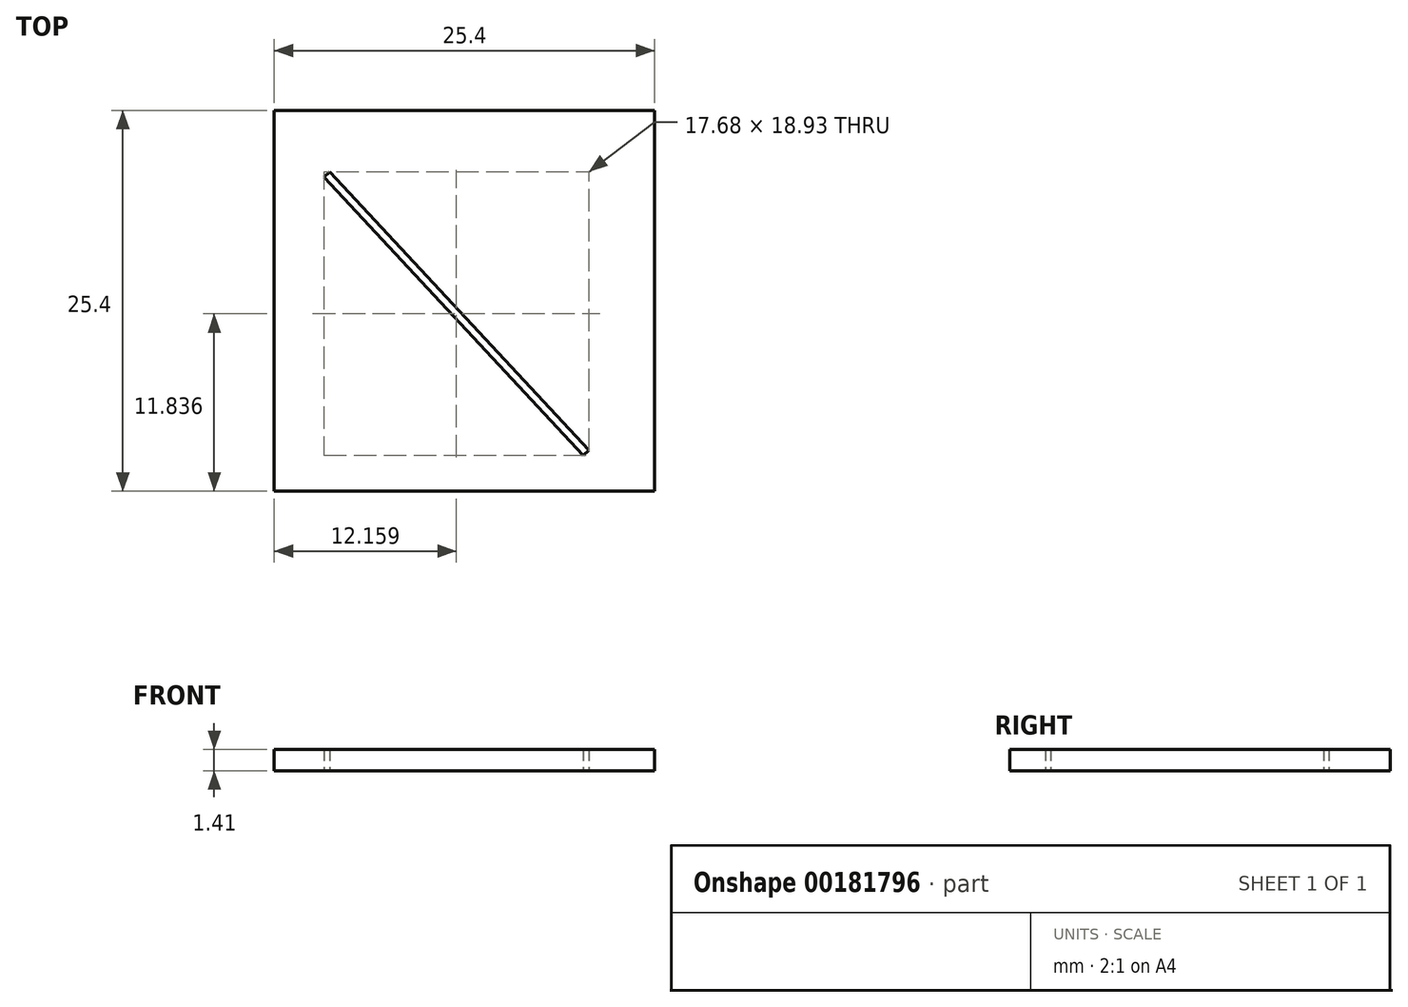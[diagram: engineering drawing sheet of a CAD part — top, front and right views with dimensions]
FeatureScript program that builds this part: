
annotation { "Feature Type Name" : "Feature", "Feature Type Description" : "" }
export const myFeature = defineFeature(function(context is Context, id is Id, definition is map)
    precondition{}
    {
        {
            var Q0;
            Q0=qCreatedBy(makeId("Top.planeOp"),FACE);
            var sketch = newSketch(context, id + "F0", { "sketchPlane" : qUnion([Q0])});
            skLineSegment(sketch, "E0.bottom", {"start": v(0, 0) * mm, "end": v(25.4, 0) * mm});
            skLineSegment(sketch, "E0.top", {"start": v(0, 25.4) * mm, "end": v(25.4, 25.4) * mm});
            skLineSegment(sketch, "E0.left", {"start": v(0, 0) * mm, "end": v(0, 25.4) * mm});
            skLineSegment(sketch, "E0.right", {"start": v(25.4, 0) * mm, "end": v(25.4, 25.4) * mm});
            skLineSegment(sketch, "E1", {"start": v(3.32, 20.95) * mm, "end": v(20.63, 2.37) * mm});
            skLineSegment(sketch, "E2", {"start": v(20.63, 2.37) * mm, "end": v(21, 2.72) * mm});
            skLineSegment(sketch, "E3", {"start": v(21, 2.72) * mm, "end": v(3.69, 21.3) * mm});
            skLineSegment(sketch, "E4", {"start": v(3.69, 21.3) * mm, "end": v(3.32, 20.95) * mm});
            skSolve(sketch);
        }
        {
            var Q0;
            Q0 = qSketchRegion(id + "F0", true);
            extrude(context, id + "F1", {"entities" : qUnion([Q0]), "depth" : 1.41 * mm});
        }
    });
